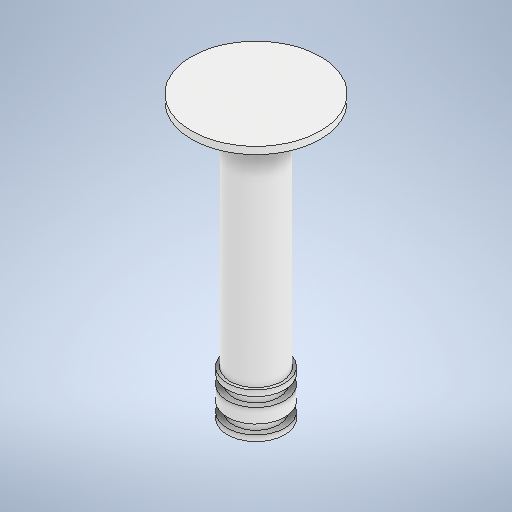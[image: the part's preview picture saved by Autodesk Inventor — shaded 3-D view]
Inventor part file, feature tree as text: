
AUTODESK INVENTOR PART (.ipt)
format: ipt  version: 2025.2 (Build 292293000, 293)  size: 278,528 bytes
history: native  units: mm
features: extrude x7, sketch x7
ambient origin geometry x8: Origin, YZ Plane, XZ Plane, XY Plane, X Axis, Y Axis, Z Axis, Center Point
bodies: Solid1 (feature_tree)
feature tree (14):
  extrude  "Extrusion1"  Depth=80.0mm TaperAngle=0.0deg
  extrude  "Extrusion2"  Depth=2.5mm TaperAngle=0.0deg
  extrude  "Extrusion3"  Depth=2.0mm TaperAngle=0.0deg
  extrude  "Extrusion4"  Depth=3.3mm TaperAngle=0.0deg
  extrude  "Extrusion5"  Depth=5.0mm TaperAngle=0.0deg
  extrude  "Extrusion6"  Depth=3.3mm TaperAngle=0.0deg
  extrude  "Extrusion7"  Depth=2.0mm TaperAngle=0.0deg
  sketch  "Sketch1"  dims[d0=18.0mm d1=80.0mm d2=0.0mm]
  sketch  "Sketch2"  dims[d3=45.0mm d4=2.5mm d5=0.0mm]
  sketch  "Sketch3"  dims[d6=20.0mm d7=2.0mm d8=0.0mm]
  sketch  "Sketch4"  dims[d9=16.0mm d10=3.3mm d11=0.0mm]
  sketch  "Sketch5"  dims[d12=20.0mm d13=5.0mm d14=0.0mm]
  sketch  "Sketch7"  dims[d15=16.0mm d16=3.3mm d17=0.0mm]
  sketch  "Sketch8"  dims[d18=20.0mm d19=2.0mm d20=0.0mm]
